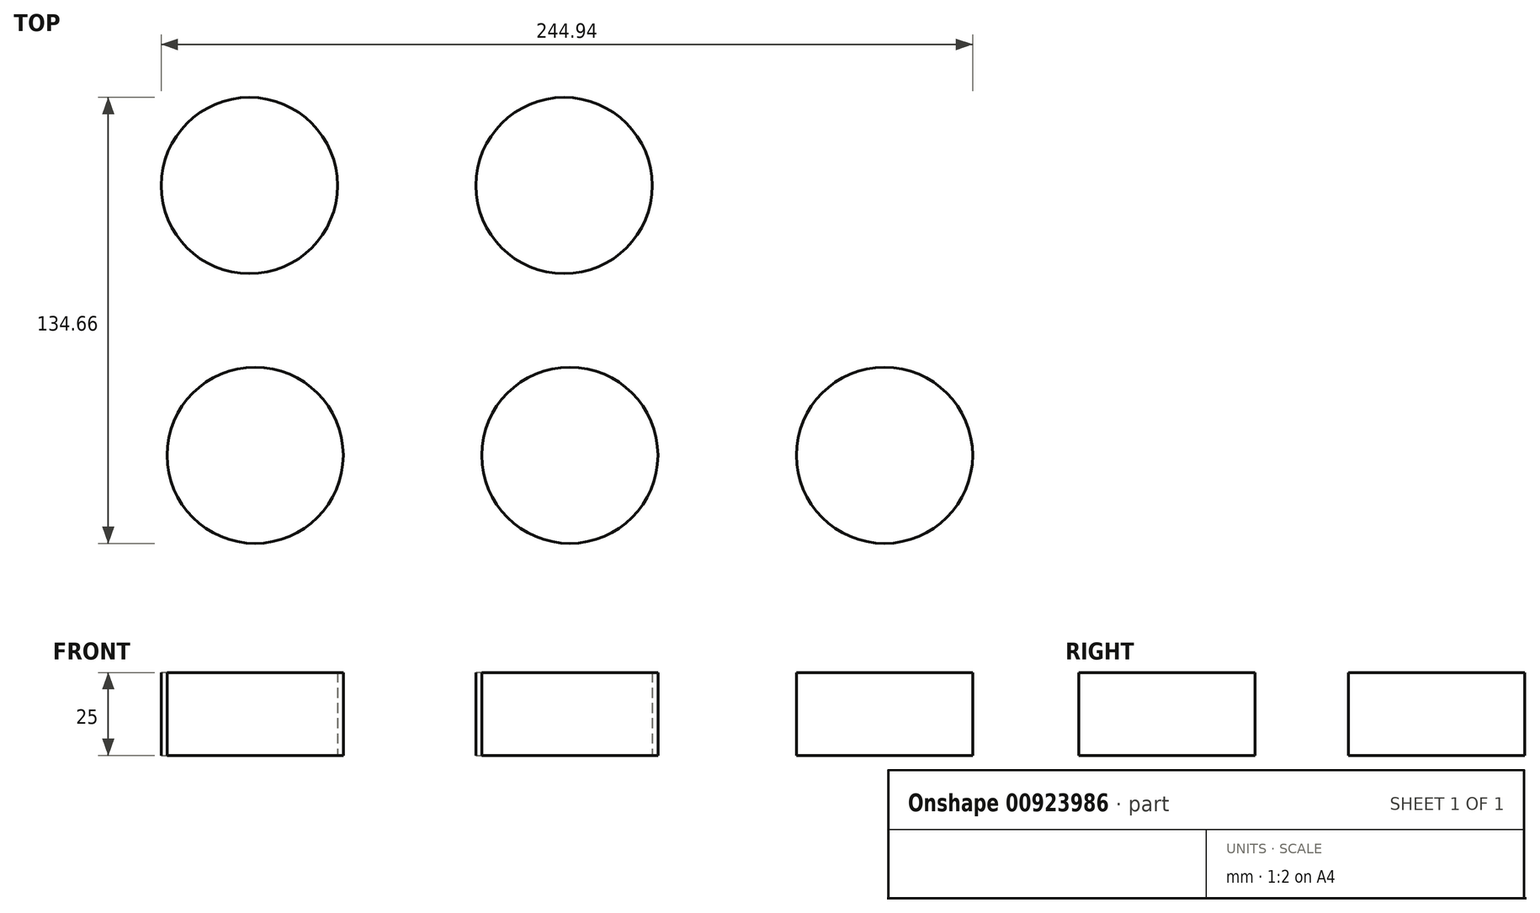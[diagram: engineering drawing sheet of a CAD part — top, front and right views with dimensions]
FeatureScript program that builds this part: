
annotation { "Feature Type Name" : "Feature", "Feature Type Description" : "" }
export const myFeature = defineFeature(function(context is Context, id is Id, definition is map)
    precondition{}
    {
        {
            var Q0;
            Q0=qCreatedBy(makeId("Top.planeOp"),FACE);
            var sketch = newSketch(context, id + "F0", { "sketchPlane" : qUnion([Q0])});
            skLineSegment(sketch, "E0.bottom", {"start": v(-146.22, -70.46) * mm, "end": v(153.78, -70.46) * mm});
            skLineSegment(sketch, "E0.top", {"start": v(-146.22, 89.54) * mm, "end": v(153.78, 89.54) * mm});
            skLineSegment(sketch, "E0.left", {"start": v(-146.22, -70.46) * mm, "end": v(-146.22, 89.54) * mm});
            skLineSegment(sketch, "E0.right", {"start": v(153.78, -70.46) * mm, "end": v(153.78, 89.54) * mm});
            skSolve(sketch);
        }
        {
            var Q0;
            Q0 = qSketchRegion(id + "F0", true);
            extrude(context, id + "F1", {"entities" : qUnion([Q0]), "depth" : 25 * mm, "offsetDistance" : 25 * mm});
        }
        {
            var Q0;
            Q0=makeQuery(id+"F1.opExtrude","CAP_FACE",FACE,{"disambiguationData":[OSD([sQuery(id+"F0.wireOp",EDGE,"E0.bottom"),sQuery(id+"F0.wireOp",EDGE,"E0.top"),sQuery(id+"F0.wireOp",EDGE,"E0.left"),sQuery(id+"F0.wireOp",EDGE,"E0.right")])],"isStart":true});
            var sketch = newSketch(context, id + "F2", { "sketchPlane" : qUnion([Q0])});
            skCircle(sketch, "E1", {"center": v(92.27, -50.45) * mm, "radius": 26.6 * mm});
            skCircle(sketch, "E2.0.1.0", {"center": v(94, 31) * mm, "radius": 26.6 * mm});
            skCircle(sketch, "E2.1.0.0", {"center": v(-2.73, -50.45) * mm, "radius": 26.6 * mm});
            skCircle(sketch, "E2.1.1.0", {"center": v(-1, 31) * mm, "radius": 26.6 * mm});
            skCircle(sketch, "E2.2.0.0", {"center": v(-97.73, -50.45) * mm, "radius": 26.6 * mm});
            skCircle(sketch, "E2.2.1.0", {"center": v(-96, 31) * mm, "radius": 26.6 * mm});
            skLineSegment(sketch, "E2.direction1", {"start": v(92.27, -50.45) * mm, "end": v(-2.73, -50.45) * mm, "construction": true});
            skLineSegment(sketch, "E2.direction2", {"start": v(92.27, -50.45) * mm, "end": v(94, 31) * mm, "construction": true});
            skSolve(sketch);
        }
        {
            var Q0;
            Q0=makeQuery(id+"F2.imprint","IMPRINT",FACE,{"disambiguationData":[TD([[makeQuery(id+"F2.imprint","IMPRINT",EDGE,{"derivedFrom":sQuery(id+"F2.wireOp",EDGE,"E1")}),1.0]])]});
            var Q1;
            Q1=makeQuery(id+"F1.opExtrude","CAP_FACE",FACE,{"disambiguationData":[OSD([sQuery(id+"F0.wireOp",EDGE,"E0.bottom"),sQuery(id+"F0.wireOp",EDGE,"E0.top"),sQuery(id+"F0.wireOp",EDGE,"E0.left"),sQuery(id+"F0.wireOp",EDGE,"E0.right")])],"isStart":false});
            var Q2;
            Q2=makeQuery(id+"F2.imprint","IMPRINT",FACE,{"disambiguationData":[TD([[makeQuery(id+"F2.imprint","IMPRINT",EDGE,{"derivedFrom":sQuery(id+"F2.wireOp",EDGE,"E1")}),-1.0]])]});
            extrude(context, id + "F3", {"entities" : qUnion([Q0, Q1, Q2]), "operationType" : NewBodyOperationType.REMOVE, "endBound" : BoundingType.THROUGH_ALL, "oppositeDirection" : true, "depth" : 25 * mm, "offsetDistance" : 25 * mm});
        }
    });
